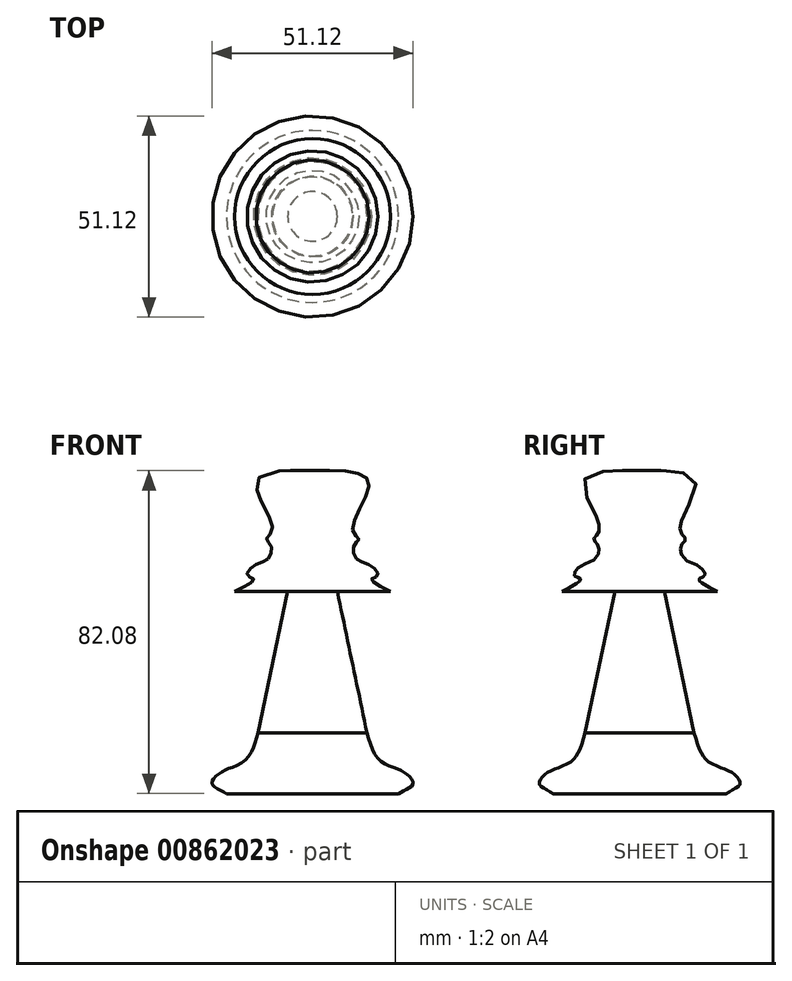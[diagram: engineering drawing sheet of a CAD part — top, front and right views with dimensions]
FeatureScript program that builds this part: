
annotation { "Feature Type Name" : "Feature", "Feature Type Description" : "" }
export const myFeature = defineFeature(function(context is Context, id is Id, definition is map)
    precondition{}
    {
        {
            var Q0;
            Q0=qCreatedBy(makeId("Front.planeOp"),FACE);
            var sketch = newSketch(context, id + "F0", { "sketchPlane" : qUnion([Q0])});
            skLineSegment(sketch, "E0", {"start": v(0, 50.48) * mm, "end": v(0, -50.48) * mm});
            skLineSegment(sketch, "E1", {"start": v(13.85, -25.3) * mm, "end": v(6.3, 10.64) * mm});
            skLineSegment(sketch, "E2", {"start": v(6.3, 10.64) * mm, "end": v(19.8, 10.64) * mm});
            skFitSpline(sketch, "E3", {"points": [v(19.8, 10.64) * mm, v(15, 13.85) * mm, v(16.6, 14.77) * mm, v(14.77, 17.28) * mm, v(11.1, 19.12) * mm, v(10.64, 22.55) * mm, v(11.79, 23.92) * mm, v(10.19, 26.44) * mm, v(14.3, 38.34) * mm, v(0, 41.32) * mm], "startDerivative": vector(-63.77, 32.33) * mm, "endDerivative": vector(-107.17, -2.4) * mm});
            skPoint(sketch, "E4.4.internal.orphan", {"position": v(25.98, -30.1) * mm});
            skPoint(sketch, "E5.start.orphan", {"position": v(19.8, -25.3) * mm});
            skPoint(sketch, "E6.end.orphan", {"position": v(25.98, -43.15) * mm});
            skLineSegment(sketch, "E7", {"start": v(0, -40.7) * mm, "end": v(21.86, -40.7) * mm});
            skFitSpline(sketch, "E8", {"points": [v(21.86, -40.7) * mm, v(23.9, -39.6) * mm, v(25.54, -38.24) * mm, v(24.59, -36.34) * mm, v(21.86, -34.57) * mm, v(16.96, -32.12) * mm, v(13.85, -25.3) * mm], "startDerivative": vector(14.56, 7.79) * mm, "endDerivative": vector(-9.27, 32.76) * mm});
            skSolve(sketch);
        }
        {
            var Q0;
            Q0 = qSketchRegion(id + "F0", true);
            var Q1;
            Q1=sQuery(id+"F0.wireOp",EDGE,"E0");
            revolve(context, id + "F1", {"surfaceOperationType" : NewSurfaceOperationType.NEW, "entities" : qUnion([Q0]), "axis" : qUnion([Q1]), "revolveType" : RevolveType.FULL});
        }
    });
